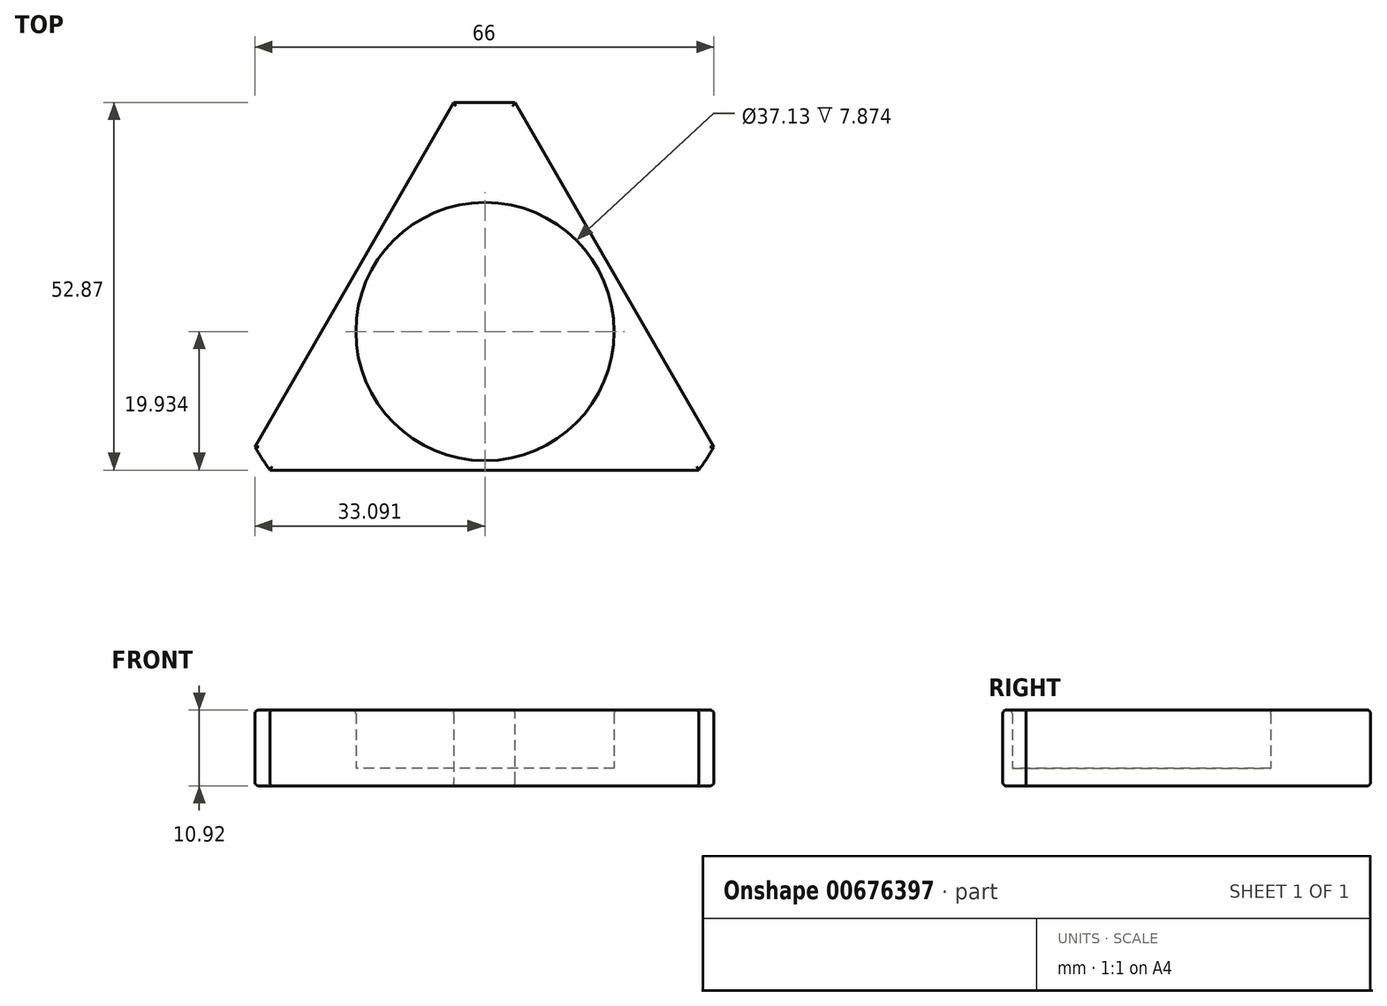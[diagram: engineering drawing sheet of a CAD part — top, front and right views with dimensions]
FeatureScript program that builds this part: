
annotation { "Feature Type Name" : "Feature", "Feature Type Description" : "" }
export const myFeature = defineFeature(function(context is Context, id is Id, definition is map)
    precondition{}
    {
        {
            var Q0;
            Q0=qCreatedBy(makeId("Top.planeOp"),FACE);
            var sketch = newSketch(context, id + "F0", { "sketchPlane" : qUnion([Q0])});
            skCircle(sketch, "E0", {"center": v(0, 0) * mm, "radius": 38.1 * mm});
            skLineSegment(sketch, "E1", {"start": v(-38.1, 0) * mm, "end": v(38.1, 0) * mm, "construction": true});
            skLineSegment(sketch, "E2", {"start": v(0, 38.1) * mm, "end": v(0, -38.1) * mm, "construction": true});
            skLineSegment(sketch, "E3.0", {"start": v(0, 38.1) * mm, "end": v(34.93, -22.4) * mm});
            skLineSegment(sketch, "E3.1", {"start": v(34.92, -22.4) * mm, "end": v(-34.93, -22.4) * mm});
            skLineSegment(sketch, "E3.2", {"start": v(-34.93, -22.4) * mm, "end": v(0, 38.1) * mm});
            skPoint(sketch, "E3.0.midPoint", {"position": v(17.46, 7.85) * mm});
            skCircle(sketch, "E4", {"center": v(0.1, -2.46) * mm, "radius": 18.57 * mm});
            skSolve(sketch);
        }
        {
            var Q0;
            Q0=makeQuery(id+"F0.imprint","IMPRINT",FACE,{"disambiguationData":[TD([[makeQuery(id+"F0.imprint","IMPRINT",EDGE,{"derivedFrom":sQuery(id+"F0.wireOp",EDGE,"E4")}),-1.0]])]});
            extrude(context, id + "F1", {"entities" : qUnion([Q0]), "depth" : 10.92 * mm, "offsetDistance" : 25.4 * mm});
        }
        {
            var Q0;
            Q0=qCreatedBy(makeId("Top.planeOp"),FACE);
            var sketch = newSketch(context, id + "F2", { "sketchPlane" : qUnion([Q0])});
            skCircle(sketch, "E5", {"center": v(0, -2.4) * mm, "radius": 19.69 * mm});
            skSolve(sketch);
        }
        {
            var Q0;
            Q0 = qSketchRegion(id + "F2", true);
            extrude(context, id + "F3", {"entities" : qUnion([Q0]), "operationType" : NewBodyOperationType.ADD, "depth" : 2.54 * mm, "offsetDistance" : 25.4 * mm});
        }
        {
            var Q0;
            Q0=makeQuery(id+"F1.opExtrude","SWEPT_EDGE",EDGE,{"disambiguationData":[OSD([sQuery(id+"F0.wireOp",EDGE,"E0"),sQuery(id+"F0.wireOp",EDGE,"E3.0"),sQuery(id+"F0.wireOp",EDGE,"E3.2")])]});
            chamfer(context, id + "F4", {"entities" : qUnion([Q0]), "width" : 5.08 * mm, "tangentPropagation" : true});
        }
        {
            var Q0;
            Q0=makeQuery(id+"F1.opExtrude","CAP_FACE",FACE,{"disambiguationData":[OSD([sQuery(id+"F0.wireOp",EDGE,"E0"),sQuery(id+"F0.wireOp",EDGE,"E3.0"),sQuery(id+"F0.wireOp",EDGE,"E3.1"),sQuery(id+"F0.wireOp",EDGE,"E3.2"),sQuery(id+"F0.wireOp",EDGE,"E4")])],"isStart":false});
            var Q1;
            Q1=makeQuery(id+"F3.boolean.opBoolean","MERGE",FACE,{"derivedFrom":[makeQuery(id+"F1.opExtrude","CAP_FACE",FACE,{"disambiguationData":[OSD([sQuery(id+"F0.wireOp",EDGE,"E0"),sQuery(id+"F0.wireOp",EDGE,"E3.0"),sQuery(id+"F0.wireOp",EDGE,"E3.1"),sQuery(id+"F0.wireOp",EDGE,"E3.2"),sQuery(id+"F0.wireOp",EDGE,"E4")])],"isStart":true}),makeQuery(id+"F3.opExtrude","CAP_FACE",FACE,{"disambiguationData":[OSD([sQuery(id+"F2.wireOp",EDGE,"E5")])],"isStart":true})]});
            fillet(context, id + "F5", {"entities" : qUnion([Q0, Q1]), "radius" : 0.5 * mm, "tangentPropagation" : true, "allowEdgeOverflow" : false});
        }
    });
